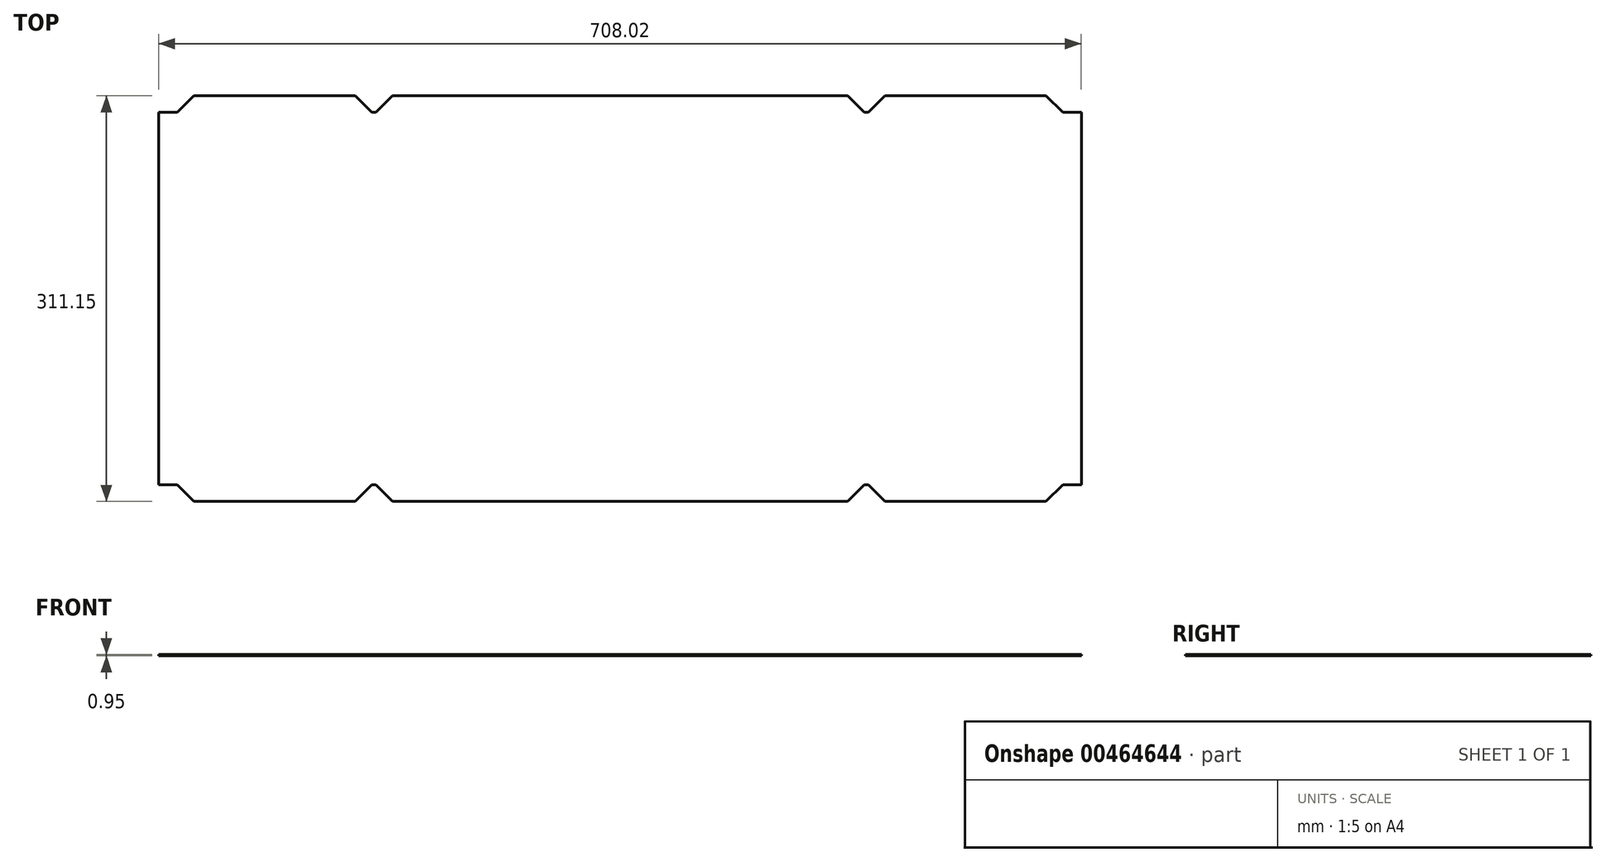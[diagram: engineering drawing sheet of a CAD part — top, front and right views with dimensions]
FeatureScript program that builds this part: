
annotation { "Feature Type Name" : "Feature", "Feature Type Description" : "" }
export const myFeature = defineFeature(function(context is Context, id is Id, definition is map)
    precondition{}
    {
        {
            var Q0;
            Q0=qCreatedBy(makeId("Top.planeOp"),FACE);
            var sketch = newSketch(context, id + "F0", { "sketchPlane" : qUnion([Q0])});
            skLineSegment(sketch, "E0.bottom", {"start": v(0, 0) * mm, "end": v(188.91, 0) * mm});
            skLineSegment(sketch, "E0.top", {"start": v(0, -285.75) * mm, "end": v(188.91, -285.75) * mm});
            skLineSegment(sketch, "E0.left", {"start": v(0, 0) * mm, "end": v(0, -285.75) * mm});
            skLineSegment(sketch, "E1", {"start": v(1.59, 0) * mm, "end": v(14.29, 12.7) * mm});
            skLineSegment(sketch, "E2", {"start": v(14.29, 12.7) * mm, "end": v(188.91, 12.7) * mm});
            skLineSegment(sketch, "E3", {"start": v(0, 0) * mm, "end": v(-152.4, 0) * mm});
            skLineSegment(sketch, "E4", {"start": v(-152.4, 0) * mm, "end": v(-152.4, -285.75) * mm});
            skLineSegment(sketch, "E5", {"start": v(-152.4, -285.75) * mm, "end": v(0, -285.75) * mm});
            skLineSegment(sketch, "E6", {"start": v(-150.81, 0) * mm, "end": v(-138.11, 12.7) * mm});
            skLineSegment(sketch, "E7", {"start": v(-138.11, 12.7) * mm, "end": v(-14.29, 12.7) * mm});
            skLineSegment(sketch, "E8", {"start": v(-14.29, 12.7) * mm, "end": v(-1.59, 0) * mm});
            skLineSegment(sketch, "E9", {"start": v(188.91, 0) * mm, "end": v(188.91, -285.75) * mm, "construction": true});
            skLineSegment(sketch, "E10", {"start": v(-152.4, -142.87) * mm, "end": v(188.91, -142.87) * mm, "construction": true});
            skLineSegment(sketch, "E11", {"start": v(188.91, 0) * mm, "end": v(188.91, 12.7) * mm, "construction": true});
            skLineSegment(sketch, "E12", {"start": v(-152.4, 0) * mm, "end": v(-165.1, 0) * mm});
            skLineSegment(sketch, "E13", {"start": v(-165.1, 0) * mm, "end": v(-165.1, -285.75) * mm});
            skLineSegment(sketch, "E14", {"start": v(-152.4, -285.75) * mm, "end": v(-165.1, -285.75) * mm});
            skLineSegment(sketch, "E15.MirrorCS", {"start": v(530.23, 0) * mm, "end": v(542.93, 0) * mm});
            skLineSegment(sketch, "E16.MirrorCS", {"start": v(530.22, -285.75) * mm, "end": v(542.92, -285.75) * mm});
            skLineSegment(sketch, "E17.MirrorCS", {"start": v(392.11, 12.7) * mm, "end": v(379.41, 0) * mm});
            skLineSegment(sketch, "E18.MirrorCS", {"start": v(528.64, 0) * mm, "end": v(515.94, 12.7) * mm});
            skLineSegment(sketch, "E19.MirrorCS", {"start": v(376.24, 0) * mm, "end": v(363.54, 12.7) * mm});
            skLineSegment(sketch, "E20.MirrorCS", {"start": v(515.94, 12.7) * mm, "end": v(392.11, 12.7) * mm});
            skLineSegment(sketch, "E21.MirrorCS", {"start": v(530.23, 0) * mm, "end": v(530.23, -285.75) * mm});
            skLineSegment(sketch, "E22.MirrorCS", {"start": v(530.23, -285.75) * mm, "end": v(377.83, -285.75) * mm});
            skLineSegment(sketch, "E23.MirrorCS", {"start": v(377.83, 0) * mm, "end": v(377.83, -285.75) * mm});
            skLineSegment(sketch, "E24.MirrorCS", {"start": v(542.92, 0) * mm, "end": v(542.92, -285.75) * mm});
            skLineSegment(sketch, "E25.MirrorCS", {"start": v(377.83, 0) * mm, "end": v(530.23, 0) * mm});
            skLineSegment(sketch, "E26.MirrorCS", {"start": v(377.83, -285.75) * mm, "end": v(188.91, -285.75) * mm});
            skLineSegment(sketch, "E27.MirrorCS", {"start": v(363.54, 12.7) * mm, "end": v(188.91, 12.7) * mm});
            skLineSegment(sketch, "E28.MirrorCS", {"start": v(377.83, 0) * mm, "end": v(188.91, 0) * mm});
            skLineSegment(sketch, "E29.MirrorCS", {"start": v(1.59, -285.75) * mm, "end": v(14.29, -298.45) * mm});
            skLineSegment(sketch, "E30.MirrorCS", {"start": v(-14.29, -298.45) * mm, "end": v(-1.59, -285.75) * mm});
            skLineSegment(sketch, "E31.MirrorCS", {"start": v(14.29, -298.45) * mm, "end": v(188.91, -298.45) * mm});
            skLineSegment(sketch, "E32.MirrorCS", {"start": v(363.54, -298.45) * mm, "end": v(188.91, -298.45) * mm});
            skLineSegment(sketch, "E33.MirrorCS", {"start": v(188.91, -285.75) * mm, "end": v(188.91, -298.45) * mm, "construction": true});
            skLineSegment(sketch, "E34.MirrorCS", {"start": v(515.94, -298.45) * mm, "end": v(392.11, -298.45) * mm});
            skLineSegment(sketch, "E35.MirrorCS", {"start": v(392.11, -298.45) * mm, "end": v(379.41, -285.75) * mm});
            skLineSegment(sketch, "E36.MirrorCS", {"start": v(528.64, -285.75) * mm, "end": v(515.94, -298.45) * mm});
            skLineSegment(sketch, "E37.MirrorCS", {"start": v(376.24, -285.75) * mm, "end": v(363.54, -298.45) * mm});
            skLineSegment(sketch, "E38.MirrorCS", {"start": v(-150.81, -285.75) * mm, "end": v(-138.11, -298.45) * mm});
            skLineSegment(sketch, "E39.MirrorCS", {"start": v(-138.11, -298.45) * mm, "end": v(-14.29, -298.45) * mm});
            skSolve(sketch);
        }
        {
            var Q0;
            Q0 = qSketchRegion(id + "F0", true);
            extrude(context, id + "F1", {"entities" : qUnion([Q0]), "depth" : 0.95 * mm});
        }
    });
